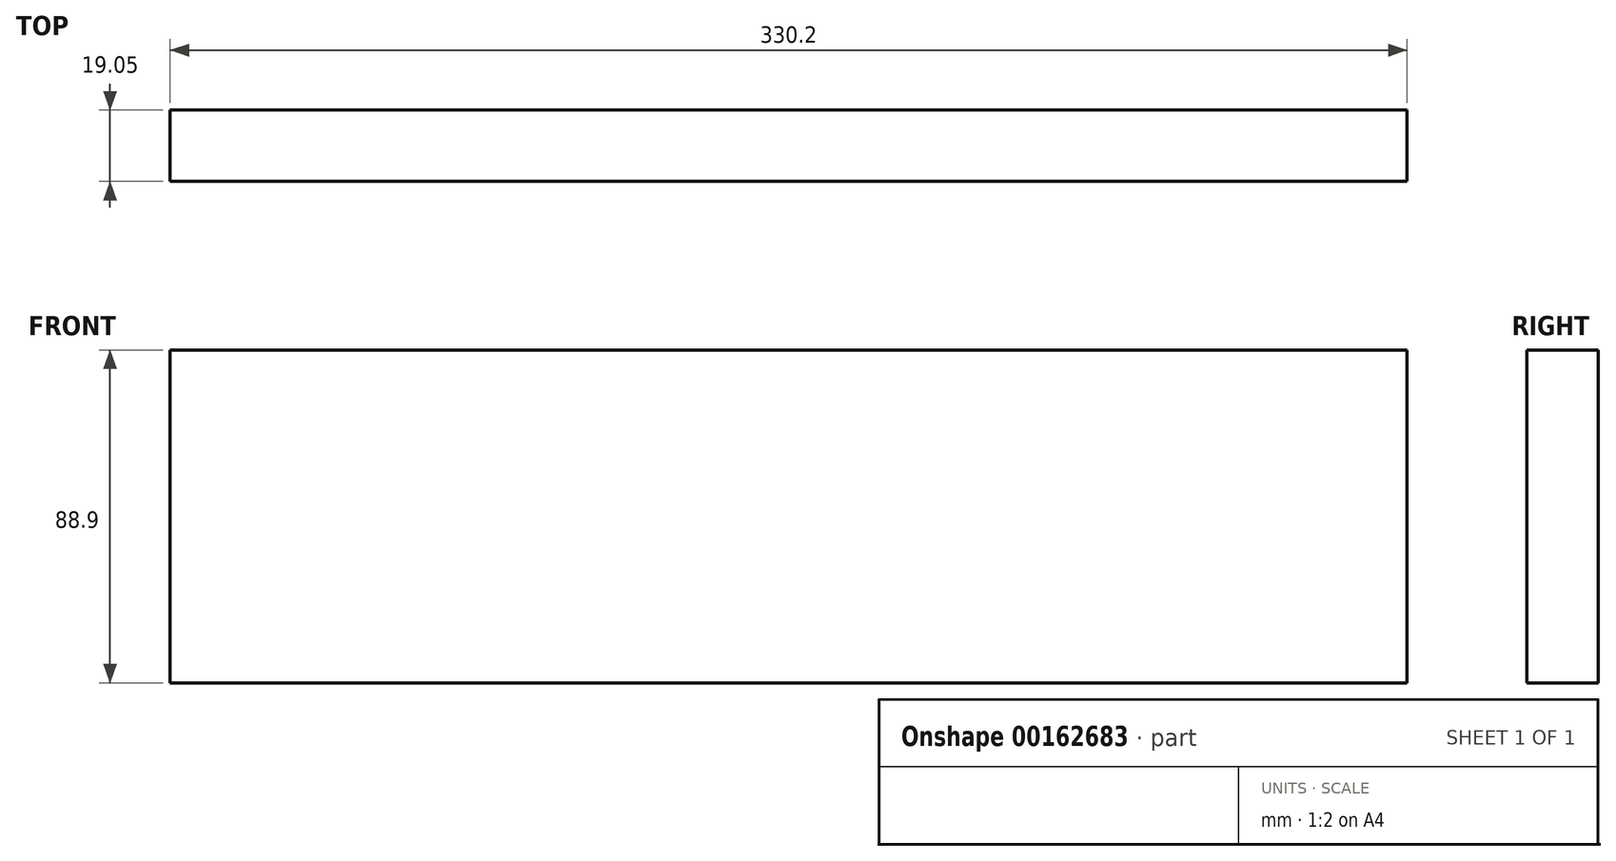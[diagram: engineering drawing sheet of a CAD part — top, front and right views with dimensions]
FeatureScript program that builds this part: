
annotation { "Feature Type Name" : "Feature", "Feature Type Description" : "" }
export const myFeature = defineFeature(function(context is Context, id is Id, definition is map)
    precondition{}
    {
        {
            var Q0;
            Q0=qCreatedBy(makeId("Front.planeOp"),FACE);
            var sketch = newSketch(context, id + "F0", { "sketchPlane" : qUnion([Q0])});
            skLineSegment(sketch, "E0.bottom", {"start": v(-157.45, 45.91) * mm, "end": v(172.75, 45.91) * mm});
            skLineSegment(sketch, "E0.top", {"start": v(-157.45, -42.99) * mm, "end": v(172.75, -42.99) * mm});
            skLineSegment(sketch, "E0.left", {"start": v(-157.45, 45.91) * mm, "end": v(-157.45, -42.99) * mm});
            skLineSegment(sketch, "E0.right", {"start": v(172.75, 45.91) * mm, "end": v(172.75, -42.99) * mm});
            skSolve(sketch);
        }
        {
            var Q0;
            Q0 = qSketchRegion(id + "F0", true);
            extrude(context, id + "F1", {"entities" : qUnion([Q0]), "depth" : 19.05 * mm});
        }
    });
